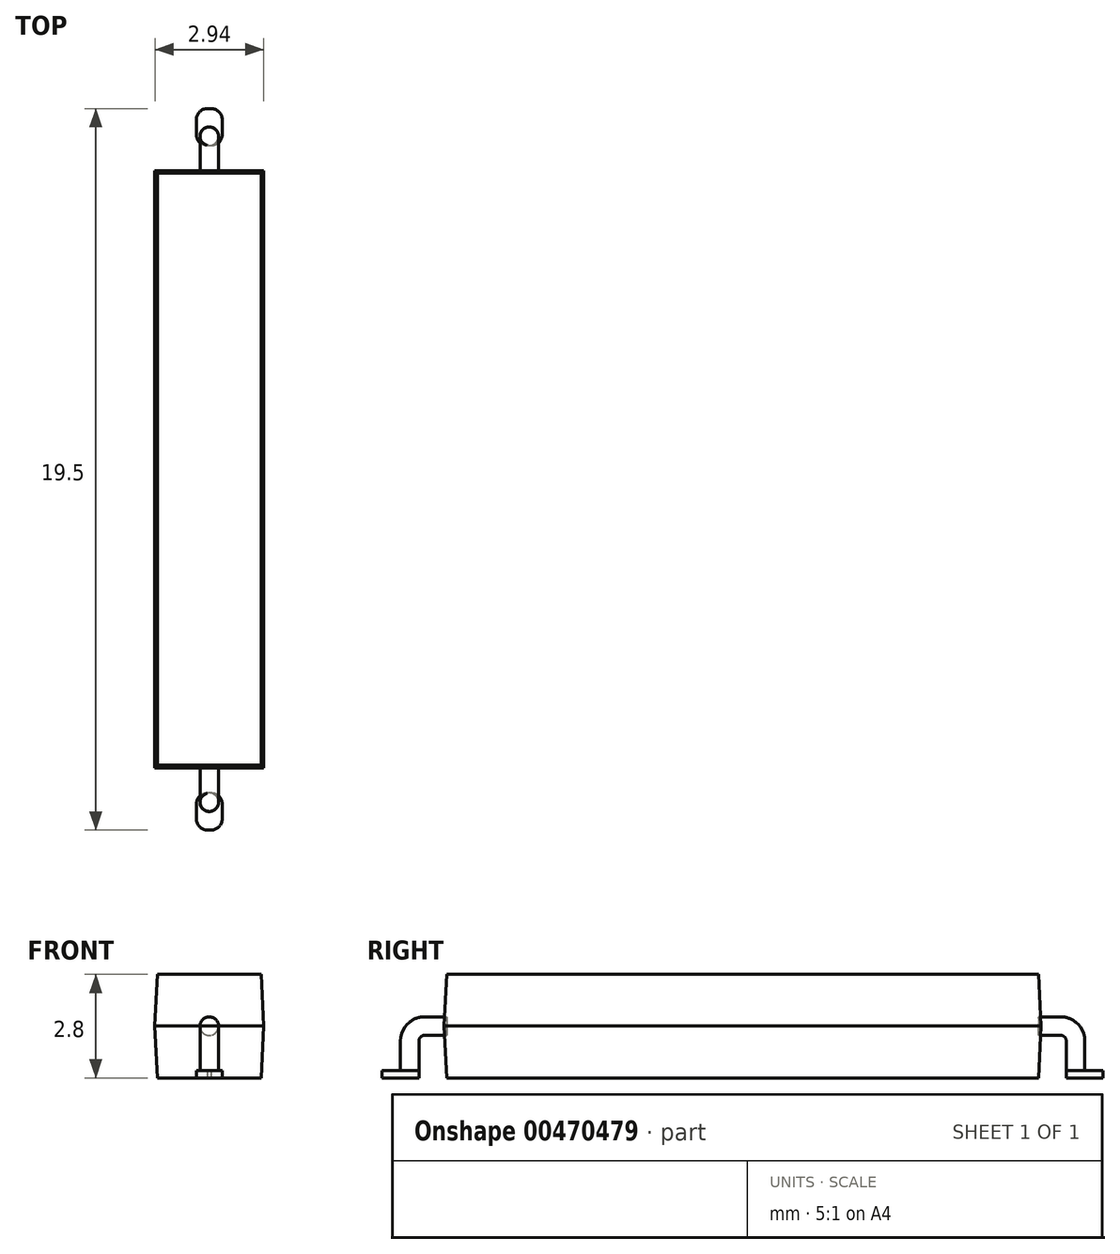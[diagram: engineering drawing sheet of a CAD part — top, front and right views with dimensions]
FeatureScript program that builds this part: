
annotation { "Feature Type Name" : "Feature", "Feature Type Description" : "" }
export const myFeature = defineFeature(function(context is Context, id is Id, definition is map)
    precondition{}
    {
        {
            var Q0;
            Q0=qCreatedBy(makeId("Top.planeOp"),FACE);
            var sketch = newSketch(context, id + "F0", { "sketchPlane" : qUnion([Q0])});
            skLineSegment(sketch, "E0.bottom", {"start": v(1.4, 8) * mm, "end": v(-1.4, 8) * mm});
            skLineSegment(sketch, "E0.top", {"start": v(1.4, -8) * mm, "end": v(-1.4, -8) * mm});
            skLineSegment(sketch, "E0.left", {"start": v(1.4, 8) * mm, "end": v(1.4, -8) * mm});
            skLineSegment(sketch, "E0.right", {"start": v(-1.4, 8) * mm, "end": v(-1.4, -8) * mm});
            skPoint(sketch, "E0.middle", {"position": v(0, 0) * mm});
            skSolve(sketch);
        }
        {
            var Q0;
            Q0 = qSketchRegion(id + "F0", true);
            extrude(context, id + "F1", {"entities" : qUnion([Q0]), "depth" : 1.4 * mm, "hasDraft" : true, "draftAngle" : 3 * degree});
        }
        {
            var Q0;
            Q0=makeQuery(id+"F1.opExtrude","CAP_FACE",FACE,{"disambiguationData":[OSD([sQuery(id+"F0.wireOp",EDGE,"E0.bottom"),sQuery(id+"F0.wireOp",EDGE,"E0.top"),sQuery(id+"F0.wireOp",EDGE,"E0.left"),sQuery(id+"F0.wireOp",EDGE,"E0.right")])],"isStart":false});
            extrude(context, id + "F2", {"entities" : qUnion([Q0]), "operationType" : NewBodyOperationType.ADD, "depth" : 1.4 * mm, "hasDraft" : true, "draftAngle" : 3 * degree, "draftPullDirection" : true});
        }
        {
            var Q0;
            Q0=qCreatedBy(makeId("Top.planeOp"),FACE);
            var sketch = newSketch(context, id + "F3", { "sketchPlane" : qUnion([Q0])});
            skLineSegment(sketch, "E1.bottom", {"start": v(0.05, -8.75) * mm, "end": v(-0.05, -8.75) * mm});
            skLineSegment(sketch, "E1.top", {"start": v(0.05, -9.75) * mm, "end": v(-0.05, -9.75) * mm});
            skLineSegment(sketch, "E1.left", {"start": v(0.35, -9.05) * mm, "end": v(0.35, -9.45) * mm});
            skLineSegment(sketch, "E1.right", {"start": v(-0.35, -9.05) * mm, "end": v(-0.35, -9.45) * mm});
            skPoint(sketch, "E1.middle", {"position": v(0, -9.25) * mm});
            skPoint(sketch, "E2.visualSharp", {"position": v(-0.35, -8.75) * mm});
            skArc(sketch, "E2.filletArc", {"start": v(-0.05, -8.75) * mm, "mid": v(-0.26, -8.84) * mm, "end": v(-0.35, -9.05) * mm});
            skPoint(sketch, "E3.visualSharp", {"position": v(0.35, -8.75) * mm});
            skArc(sketch, "E3.filletArc", {"start": v(0.35, -9.05) * mm, "mid": v(0.26, -8.84) * mm, "end": v(0.05, -8.75) * mm});
            skPoint(sketch, "E4.visualSharp", {"position": v(0.35, -9.75) * mm});
            skArc(sketch, "E4.filletArc", {"start": v(0.05, -9.75) * mm, "mid": v(0.26, -9.66) * mm, "end": v(0.35, -9.45) * mm});
            skPoint(sketch, "E5.visualSharp", {"position": v(-0.35, -9.75) * mm});
            skArc(sketch, "E5.filletArc", {"start": v(-0.35, -9.45) * mm, "mid": v(-0.26, -9.66) * mm, "end": v(-0.05, -9.75) * mm});
            skSolve(sketch);
        }
        {
            var Q0;
            Q0=qCreatedBy(makeId("Right.planeOp"),FACE);
            var sketch = newSketch(context, id + "F4", { "sketchPlane" : qUnion([Q0])});
            skLineSegment(sketch, "E6", {"start": v(-8, 1.4) * mm, "end": v(-8.6, 1.4) * mm});
            skLineSegment(sketch, "E7", {"start": v(-9, 1) * mm, "end": v(-9, 0) * mm});
            skLineSegment(sketch, "E8", {"start": v(-8, 2.8) * mm, "end": v(-8, 0) * mm, "construction": true});
            skPoint(sketch, "E9.visualSharp", {"position": v(-9, 1.4) * mm});
            skArc(sketch, "E9.filletArc", {"start": v(-8.6, 1.4) * mm, "mid": v(-8.88, 1.28) * mm, "end": v(-9, 1) * mm});
            skSolve(sketch);
        }
        {
            var Q0;
            Q0=qCreatedBy(makeId("Top.planeOp"),FACE);
            var sketch = newSketch(context, id + "F5", { "sketchPlane" : qUnion([Q0])});
            skCircle(sketch, "E10", {"center": v(0, -9) * mm, "radius": 0.25 * mm});
            skSolve(sketch);
        }
        {
            var Q0;
            Q0=makeQuery(id+"F5.imprint","IMPRINT",FACE,{"disambiguationData":[TD([[makeQuery(id+"F5.imprint","IMPRINT",EDGE,{"derivedFrom":sQuery(id+"F5.wireOp",EDGE,"E10")}),1.0]])]});
            var Q1;
            Q1=sQuery(id+"F4.wireOp",EDGE,"E7");
            var Q2;
            Q2=sQuery(id+"F4.wireOp",EDGE,"E9.filletArc");
            var Q3;
            Q3=sQuery(id+"F4.wireOp",EDGE,"E6");
            sweep(context, id + "F6", {"profiles" : qUnion([Q0]), "path" : qUnion([Q1, Q2, Q3])});
        }
        {
            var Q0;
            Q0 = qSketchRegion(id + "F3", true);
            extrude(context, id + "F7", {"entities" : qUnion([Q0]), "operationType" : NewBodyOperationType.ADD, "depth" : .2 * mm});
        }
        {
            var Q0;
            Q0=makeQuery(id+"F6.opSweep","SWEPT_BODY",BODY,{"disambiguationData":[OSD([sQuery(id+"F4.wireOp",EDGE,"E6"),sQuery(id+"F5.wireOp",EDGE,"E10")])]});
            var Q1;
            Q1=qCreatedBy(makeId("Front.planeOp"),FACE);
            mirror(context, id + "F8", {"entities" : qUnion([Q0]), "mirrorPlane" : qUnion([Q1])});
        }
    });
